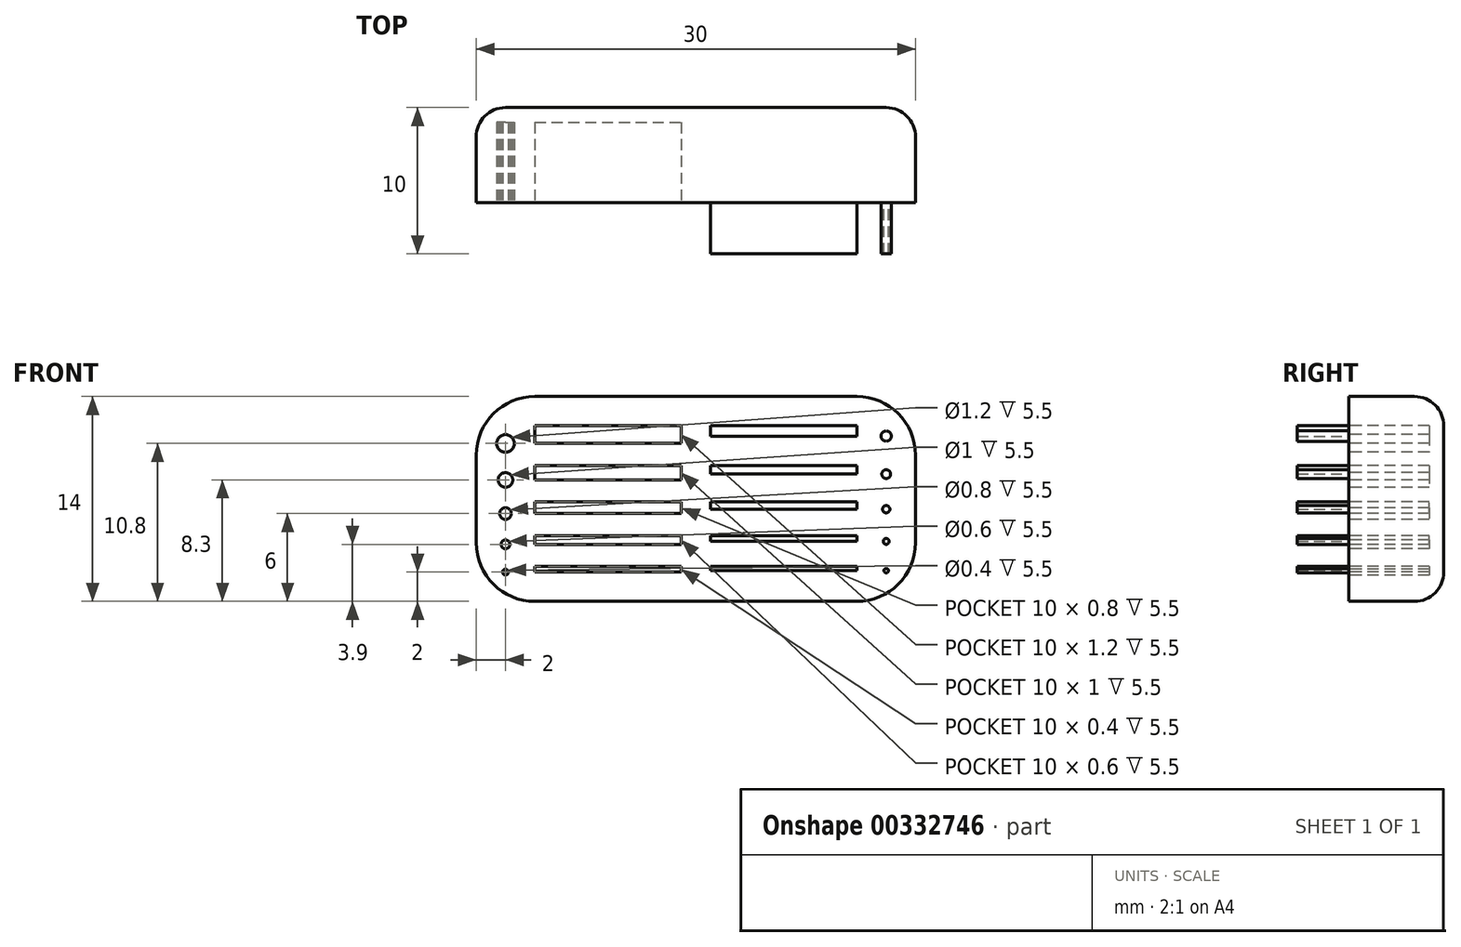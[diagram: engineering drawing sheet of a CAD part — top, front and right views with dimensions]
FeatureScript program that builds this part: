
annotation { "Feature Type Name" : "Feature", "Feature Type Description" : "" }
export const myFeature = defineFeature(function(context is Context, id is Id, definition is map)
    precondition{}
    {
        {
            var Q0;
            Q0=qCreatedBy(makeId("Front.planeOp"),FACE);
            var sketch = newSketch(context, id + "F0", { "sketchPlane" : qUnion([Q0])});
            skLineSegment(sketch, "E0.bottom", {"start": v(0, 0) * mm, "end": v(10, 0) * mm});
            skLineSegment(sketch, "E0.top", {"start": v(0, -1.2) * mm, "end": v(10, -1.2) * mm});
            skLineSegment(sketch, "E0.left", {"start": v(0, 0) * mm, "end": v(0, -1.2) * mm});
            skLineSegment(sketch, "E0.right", {"start": v(10, 0) * mm, "end": v(10, -1.2) * mm});
            skLineSegment(sketch, "E1.bottom", {"start": v(0, -2.7) * mm, "end": v(10, -2.7) * mm});
            skLineSegment(sketch, "E1.top", {"start": v(0, -3.7) * mm, "end": v(10, -3.7) * mm});
            skLineSegment(sketch, "E1.left", {"start": v(0, -2.7) * mm, "end": v(0, -3.7) * mm});
            skLineSegment(sketch, "E1.right", {"start": v(10, -2.7) * mm, "end": v(10, -3.7) * mm});
            skLineSegment(sketch, "E2.bottom", {"start": v(0, -6) * mm, "end": v(10, -6) * mm});
            skLineSegment(sketch, "E2.top", {"start": v(0, -5.2) * mm, "end": v(10, -5.2) * mm});
            skLineSegment(sketch, "E2.left", {"start": v(0, -6) * mm, "end": v(0, -5.2) * mm});
            skLineSegment(sketch, "E2.right", {"start": v(10, -6) * mm, "end": v(10, -5.2) * mm});
            skLineSegment(sketch, "E3.bottom", {"start": v(0, -8.1) * mm, "end": v(10, -8.1) * mm});
            skLineSegment(sketch, "E3.top", {"start": v(0, -7.5) * mm, "end": v(10, -7.5) * mm});
            skLineSegment(sketch, "E3.left", {"start": v(0, -8.1) * mm, "end": v(0, -7.5) * mm});
            skLineSegment(sketch, "E3.right", {"start": v(10, -8.1) * mm, "end": v(10, -7.5) * mm});
            skLineSegment(sketch, "E4.bottom", {"start": v(0, -9.6) * mm, "end": v(10, -9.6) * mm});
            skLineSegment(sketch, "E4.top", {"start": v(0, -10) * mm, "end": v(10, -10) * mm});
            skLineSegment(sketch, "E4.left", {"start": v(0, -9.6) * mm, "end": v(0, -10) * mm});
            skLineSegment(sketch, "E4.right", {"start": v(10, -9.6) * mm, "end": v(10, -10) * mm});
            skLineSegment(sketch, "E5.bottom", {"start": v(12, 0) * mm, "end": v(22, 0) * mm});
            skLineSegment(sketch, "E5.top", {"start": v(12, -0.7) * mm, "end": v(22, -0.7) * mm});
            skLineSegment(sketch, "E5.left", {"start": v(12, 0) * mm, "end": v(12, -0.7) * mm});
            skLineSegment(sketch, "E5.right", {"start": v(22, 0) * mm, "end": v(22, -0.7) * mm});
            skLineSegment(sketch, "E6.bottom", {"start": v(12, -2.7) * mm, "end": v(22, -2.7) * mm});
            skLineSegment(sketch, "E6.top", {"start": v(12, -3.3) * mm, "end": v(22, -3.3) * mm});
            skLineSegment(sketch, "E6.left", {"start": v(12, -2.7) * mm, "end": v(12, -3.3) * mm});
            skLineSegment(sketch, "E6.right", {"start": v(22, -2.7) * mm, "end": v(22, -3.3) * mm});
            skLineSegment(sketch, "E7.bottom", {"start": v(12, -5.2) * mm, "end": v(22, -5.2) * mm});
            skLineSegment(sketch, "E7.top", {"start": v(12, -5.7) * mm, "end": v(22, -5.7) * mm});
            skLineSegment(sketch, "E7.left", {"start": v(12, -5.2) * mm, "end": v(12, -5.7) * mm});
            skLineSegment(sketch, "E7.right", {"start": v(22, -5.2) * mm, "end": v(22, -5.7) * mm});
            skLineSegment(sketch, "E8.bottom", {"start": v(12, -7.5) * mm, "end": v(22, -7.5) * mm});
            skLineSegment(sketch, "E8.top", {"start": v(12, -7.9) * mm, "end": v(22, -7.9) * mm});
            skLineSegment(sketch, "E8.left", {"start": v(12, -7.5) * mm, "end": v(12, -7.9) * mm});
            skLineSegment(sketch, "E8.right", {"start": v(22, -7.5) * mm, "end": v(22, -7.9) * mm});
            skLineSegment(sketch, "E9.bottom", {"start": v(12, -9.6) * mm, "end": v(22, -9.6) * mm});
            skLineSegment(sketch, "E9.top", {"start": v(12, -9.9) * mm, "end": v(22, -9.9) * mm});
            skLineSegment(sketch, "E9.left", {"start": v(12, -9.6) * mm, "end": v(12, -9.9) * mm});
            skLineSegment(sketch, "E9.right", {"start": v(22, -9.6) * mm, "end": v(22, -9.9) * mm});
            skCircle(sketch, "E10", {"center": v(-2, -1.2) * mm, "radius": 0.6 * mm});
            skCircle(sketch, "E11", {"center": v(-2, -3.7) * mm, "radius": 0.5 * mm});
            skCircle(sketch, "E12", {"center": v(-2, -6) * mm, "radius": 0.4 * mm});
            skCircle(sketch, "E13", {"center": v(-2, -8.1) * mm, "radius": 0.3 * mm});
            skCircle(sketch, "E14", {"center": v(-2, -10) * mm, "radius": 0.2 * mm});
            skLineSegment(sketch, "E15", {"start": v(0, -1.2) * mm, "end": v(-2, -1.2) * mm, "construction": true});
            skCircle(sketch, "E16", {"center": v(24, -0.7) * mm, "radius": 0.35 * mm});
            skCircle(sketch, "E17", {"center": v(24, -3.3) * mm, "radius": 0.3 * mm});
            skCircle(sketch, "E18", {"center": v(24, -5.7) * mm, "radius": 0.25 * mm});
            skCircle(sketch, "E19", {"center": v(24, -7.9) * mm, "radius": 0.2 * mm});
            skCircle(sketch, "E20", {"center": v(24, -9.9) * mm, "radius": 0.15 * mm});
            skLineSegment(sketch, "E21.bottom", {"start": v(-4, 2) * mm, "end": v(26, 2) * mm});
            skLineSegment(sketch, "E21.top", {"start": v(-4, -12) * mm, "end": v(26, -12) * mm});
            skLineSegment(sketch, "E21.left", {"start": v(-4, 2) * mm, "end": v(-4, -12) * mm});
            skLineSegment(sketch, "E21.right", {"start": v(26, 2) * mm, "end": v(26, -12) * mm});
            skSolve(sketch);
        }
        {
            var Q0;
            Q0=makeQuery(id+"F0.imprint","IMPRINT",FACE,{"disambiguationData":[TD([[makeQuery(id+"F0.imprint","IMPRINT",EDGE,{"derivedFrom":sQuery(id+"F0.wireOp",EDGE,"E5.bottom")}),-1.0]])]});
            var Q1;
            Q1=makeQuery(id+"F0.imprint","IMPRINT",FACE,{"disambiguationData":[TD([[makeQuery(id+"F0.imprint","IMPRINT",EDGE,{"derivedFrom":sQuery(id+"F0.wireOp",EDGE,"E6.bottom")}),-1.0]])]});
            var Q2;
            Q2=makeQuery(id+"F0.imprint","IMPRINT",FACE,{"disambiguationData":[TD([[makeQuery(id+"F0.imprint","IMPRINT",EDGE,{"derivedFrom":sQuery(id+"F0.wireOp",EDGE,"E7.bottom")}),-1.0]])]});
            var Q3;
            Q3=makeQuery(id+"F0.imprint","IMPRINT",FACE,{"disambiguationData":[TD([[makeQuery(id+"F0.imprint","IMPRINT",EDGE,{"derivedFrom":sQuery(id+"F0.wireOp",EDGE,"E8.bottom")}),-1.0]])]});
            var Q4;
            Q4=makeQuery(id+"F0.imprint","IMPRINT",FACE,{"disambiguationData":[TD([[makeQuery(id+"F0.imprint","IMPRINT",EDGE,{"derivedFrom":sQuery(id+"F0.wireOp",EDGE,"E9.bottom")}),-1.0]])]});
            var Q5;
            Q5=makeQuery(id+"F0.imprint","IMPRINT",FACE,{"disambiguationData":[TD([[makeQuery(id+"F0.imprint","IMPRINT",EDGE,{"derivedFrom":sQuery(id+"F0.wireOp",EDGE,"E16")}),1.0]])]});
            var Q6;
            Q6=makeQuery(id+"F0.imprint","IMPRINT",FACE,{"disambiguationData":[TD([[makeQuery(id+"F0.imprint","IMPRINT",EDGE,{"derivedFrom":sQuery(id+"F0.wireOp",EDGE,"E17")}),1.0]])]});
            var Q7;
            Q7=makeQuery(id+"F0.imprint","IMPRINT",FACE,{"disambiguationData":[TD([[makeQuery(id+"F0.imprint","IMPRINT",EDGE,{"derivedFrom":sQuery(id+"F0.wireOp",EDGE,"E18")}),1.0]])]});
            var Q8;
            Q8=makeQuery(id+"F0.imprint","IMPRINT",FACE,{"disambiguationData":[TD([[makeQuery(id+"F0.imprint","IMPRINT",EDGE,{"derivedFrom":sQuery(id+"F0.wireOp",EDGE,"E19")}),1.0]])]});
            var Q9;
            Q9=makeQuery(id+"F0.imprint","IMPRINT",FACE,{"disambiguationData":[TD([[makeQuery(id+"F0.imprint","IMPRINT",EDGE,{"derivedFrom":sQuery(id+"F0.wireOp",EDGE,"E20")}),1.0]])]});
            var Q10;
            Q10=makeQuery(id+"F0.imprint","IMPRINT",FACE,{"disambiguationData":[TD([[makeQuery(id+"F0.imprint","IMPRINT",EDGE,{"derivedFrom":sQuery(id+"F0.wireOp",EDGE,"E0.bottom")}),1.0]])]});
            extrude(context, id + "F1", {"entities" : qUnion([Q0, Q1, Q2, Q3, Q4, Q5, Q6, Q7, Q8, Q9, Q10]), "oppositeDirection" : true, "depth" : 6.5 * mm});
        }
        {
            var Q0;
            Q0=makeQuery(id+"F0.imprint","IMPRINT",FACE,{"disambiguationData":[TD([[makeQuery(id+"F0.imprint","IMPRINT",EDGE,{"derivedFrom":sQuery(id+"F0.wireOp",EDGE,"E5.bottom")}),-1.0]])]});
            var Q1;
            Q1=makeQuery(id+"F0.imprint","IMPRINT",FACE,{"disambiguationData":[TD([[makeQuery(id+"F0.imprint","IMPRINT",EDGE,{"derivedFrom":sQuery(id+"F0.wireOp",EDGE,"E6.bottom")}),-1.0]])]});
            var Q2;
            Q2=makeQuery(id+"F0.imprint","IMPRINT",FACE,{"disambiguationData":[TD([[makeQuery(id+"F0.imprint","IMPRINT",EDGE,{"derivedFrom":sQuery(id+"F0.wireOp",EDGE,"E7.bottom")}),-1.0]])]});
            var Q3;
            Q3=makeQuery(id+"F0.imprint","IMPRINT",FACE,{"disambiguationData":[TD([[makeQuery(id+"F0.imprint","IMPRINT",EDGE,{"derivedFrom":sQuery(id+"F0.wireOp",EDGE,"E8.bottom")}),-1.0]])]});
            var Q4;
            Q4=makeQuery(id+"F0.imprint","IMPRINT",FACE,{"disambiguationData":[TD([[makeQuery(id+"F0.imprint","IMPRINT",EDGE,{"derivedFrom":sQuery(id+"F0.wireOp",EDGE,"E9.bottom")}),-1.0]])]});
            var Q5;
            Q5=makeQuery(id+"F0.imprint","IMPRINT",FACE,{"disambiguationData":[TD([[makeQuery(id+"F0.imprint","IMPRINT",EDGE,{"derivedFrom":sQuery(id+"F0.wireOp",EDGE,"E16")}),1.0]])]});
            var Q6;
            Q6=makeQuery(id+"F0.imprint","IMPRINT",FACE,{"disambiguationData":[TD([[makeQuery(id+"F0.imprint","IMPRINT",EDGE,{"derivedFrom":sQuery(id+"F0.wireOp",EDGE,"E17")}),1.0]])]});
            var Q7;
            Q7=makeQuery(id+"F0.imprint","IMPRINT",FACE,{"disambiguationData":[TD([[makeQuery(id+"F0.imprint","IMPRINT",EDGE,{"derivedFrom":sQuery(id+"F0.wireOp",EDGE,"E18")}),1.0]])]});
            var Q8;
            Q8=makeQuery(id+"F0.imprint","IMPRINT",FACE,{"disambiguationData":[TD([[makeQuery(id+"F0.imprint","IMPRINT",EDGE,{"derivedFrom":sQuery(id+"F0.wireOp",EDGE,"E19")}),1.0]])]});
            var Q9;
            Q9=makeQuery(id+"F0.imprint","IMPRINT",FACE,{"disambiguationData":[TD([[makeQuery(id+"F0.imprint","IMPRINT",EDGE,{"derivedFrom":sQuery(id+"F0.wireOp",EDGE,"E20")}),1.0]])]});
            extrude(context, id + "F2", {"entities" : qUnion([Q0, Q1, Q2, Q3, Q4, Q5, Q6, Q7, Q8, Q9]), "operationType" : NewBodyOperationType.ADD, "depth" : 3.5 * mm});
        }
        {
            var Q0;
            Q0=makeQuery(id+"F1.opExtrude","CAP_FACE",FACE,{"disambiguationData":[OSD([sQuery(id+"F0.wireOp",EDGE,"E0.bottom"),sQuery(id+"F0.wireOp",EDGE,"E0.top"),sQuery(id+"F0.wireOp",EDGE,"E0.left"),sQuery(id+"F0.wireOp",EDGE,"E0.right"),sQuery(id+"F0.wireOp",EDGE,"E1.bottom"),sQuery(id+"F0.wireOp",EDGE,"E1.top"),sQuery(id+"F0.wireOp",EDGE,"E1.left"),sQuery(id+"F0.wireOp",EDGE,"E1.right"),sQuery(id+"F0.wireOp",EDGE,"E2.bottom"),sQuery(id+"F0.wireOp",EDGE,"E2.top"),sQuery(id+"F0.wireOp",EDGE,"E2.left"),sQuery(id+"F0.wireOp",EDGE,"E2.right"),sQuery(id+"F0.wireOp",EDGE,"E3.bottom"),sQuery(id+"F0.wireOp",EDGE,"E3.top"),sQuery(id+"F0.wireOp",EDGE,"E3.left"),sQuery(id+"F0.wireOp",EDGE,"E3.right"),sQuery(id+"F0.wireOp",EDGE,"E4.bottom"),sQuery(id+"F0.wireOp",EDGE,"E4.top"),sQuery(id+"F0.wireOp",EDGE,"E4.left"),sQuery(id+"F0.wireOp",EDGE,"E4.right"),sQuery(id+"F0.wireOp",EDGE,"E10"),sQuery(id+"F0.wireOp",EDGE,"E11"),sQuery(id+"F0.wireOp",EDGE,"E12"),sQuery(id+"F0.wireOp",EDGE,"E13"),sQuery(id+"F0.wireOp",EDGE,"E14"),sQuery(id+"F0.wireOp",EDGE,"E21.bottom"),sQuery(id+"F0.wireOp",EDGE,"E21.top"),sQuery(id+"F0.wireOp",EDGE,"E21.left"),sQuery(id+"F0.wireOp",EDGE,"E21.right")])],"isStart":false});
            var sketch = newSketch(context, id + "F3", { "sketchPlane" : qUnion([Q0])});
            skLineSegment(sketch, "E22.bottom", {"start": v(4, 2) * mm, "end": v(-26, 2) * mm});
            skLineSegment(sketch, "E22.top", {"start": v(4, -12) * mm, "end": v(-26, -12) * mm});
            skLineSegment(sketch, "E22.left", {"start": v(4, 2) * mm, "end": v(4, -12) * mm});
            skLineSegment(sketch, "E22.right", {"start": v(-26, 2) * mm, "end": v(-26, -12) * mm});
            skSolve(sketch);
        }
        {
            var Q0;
            Q0 = qSketchRegion(id + "F3", true);
            extrude(context, id + "F4", {"entities" : qUnion([Q0]), "operationType" : NewBodyOperationType.ADD, "oppositeDirection" : true, "depth" : 1 * mm});
        }
        {
            var Q0;
            Q0=makeQuery(id+"F1.opExtrude","CAP_EDGE",EDGE,{"disambiguationData":[OSD([sQuery(id+"F0.wireOp",EDGE,"E21.left")])],"isStart":false});
            var Q1;
            Q1=makeQuery(id+"F1.opExtrude","CAP_EDGE",EDGE,{"disambiguationData":[OSD([sQuery(id+"F0.wireOp",EDGE,"E21.top")])],"isStart":false});
            var Q2;
            Q2=makeQuery(id+"F1.opExtrude","CAP_EDGE",EDGE,{"disambiguationData":[OSD([sQuery(id+"F0.wireOp",EDGE,"E21.right")])],"isStart":false});
            var Q3;
            Q3=makeQuery(id+"F1.opExtrude","CAP_EDGE",EDGE,{"disambiguationData":[OSD([sQuery(id+"F0.wireOp",EDGE,"E21.bottom")])],"isStart":false});
            fillet(context, id + "F5", {"entities" : qUnion([Q0, Q1, Q2, Q3]), "radius" : 2 * mm, "tangentPropagation" : true, "allowEdgeOverflow" : false});
        }
        {
            var Q0;
            Q0=makeQuery(id+"F1.opExtrude","SWEPT_EDGE",EDGE,{"disambiguationData":[OSD([sQuery(id+"F0.wireOp",EDGE,"E21.top"),sQuery(id+"F0.wireOp",EDGE,"E21.left")])]});
            var Q1;
            Q1=makeQuery(id+"F1.opExtrude","SWEPT_EDGE",EDGE,{"disambiguationData":[OSD([sQuery(id+"F0.wireOp",EDGE,"E21.bottom"),sQuery(id+"F0.wireOp",EDGE,"E21.left")])]});
            var Q2;
            Q2=makeQuery(id+"F1.opExtrude","SWEPT_EDGE",EDGE,{"disambiguationData":[OSD([sQuery(id+"F0.wireOp",EDGE,"E21.top"),sQuery(id+"F0.wireOp",EDGE,"E21.right")])]});
            var Q3;
            Q3=makeQuery(id+"F1.opExtrude","SWEPT_EDGE",EDGE,{"disambiguationData":[OSD([sQuery(id+"F0.wireOp",EDGE,"E21.bottom"),sQuery(id+"F0.wireOp",EDGE,"E21.right")])]});
            fillet(context, id + "F6", {"entities" : qUnion([Q0, Q1, Q2, Q3]), "radius" : 4 * mm, "tangentPropagation" : true, "allowEdgeOverflow" : false});
        }
    });
